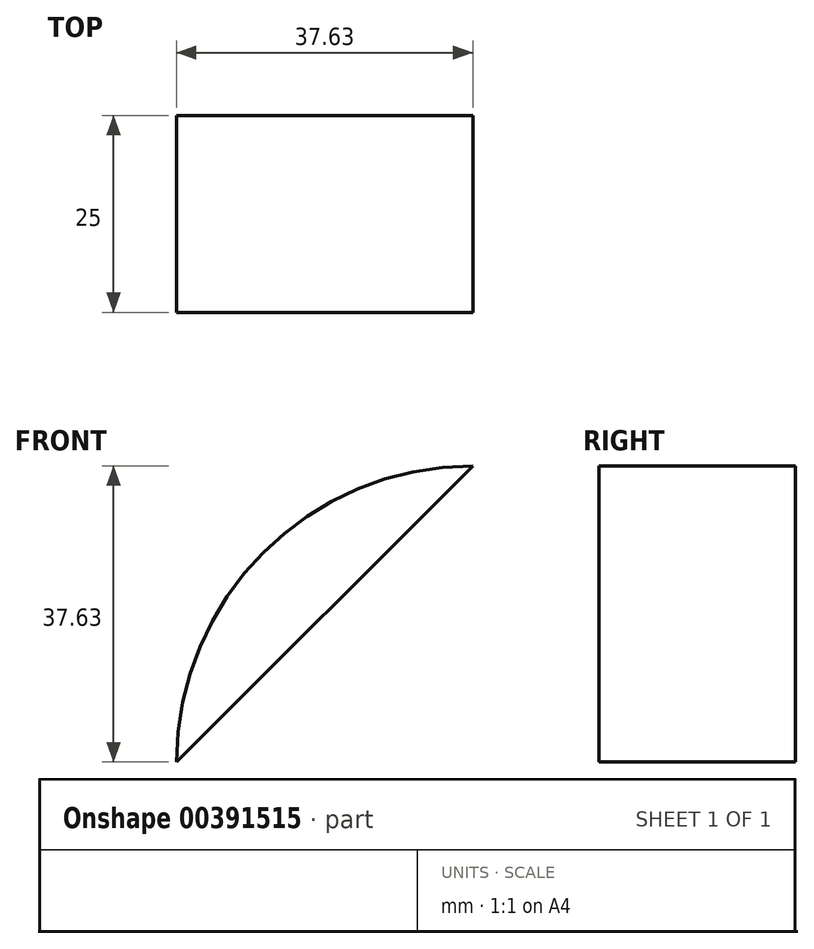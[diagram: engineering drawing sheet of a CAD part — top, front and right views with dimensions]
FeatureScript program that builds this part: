
annotation { "Feature Type Name" : "Feature", "Feature Type Description" : "" }
export const myFeature = defineFeature(function(context is Context, id is Id, definition is map)
    precondition{}
    {
        {
            var Q0;
            Q0=qCreatedBy(makeId("Front.planeOp"),FACE);
            var sketch = newSketch(context, id + "F0", { "sketchPlane" : qUnion([Q0])});
            skCircle(sketch, "E0", {"center": v(0, 0) * mm, "radius": 37.63 * mm});
            skLineSegment(sketch, "E1", {"start": v(-37.63, 0) * mm, "end": v(0, 37.63) * mm});
            skSolve(sketch);
        }
        {
            var Q0;
            {var subQ0=sQuery(id+"F0.wireOp",EDGE,"E1");Q0=makeQuery(id+"F0.imprint","IMPRINT",FACE,{"disambiguationData":[TD([[makeQuery(id+"F0.imprint","IMPRINT",EDGE,{"derivedFrom":subQ0}),1.0]])]});}
            extrude(context, id + "F1", {"entities" : qUnion([Q0]), "depth" : 25 * mm});
        }
    });
